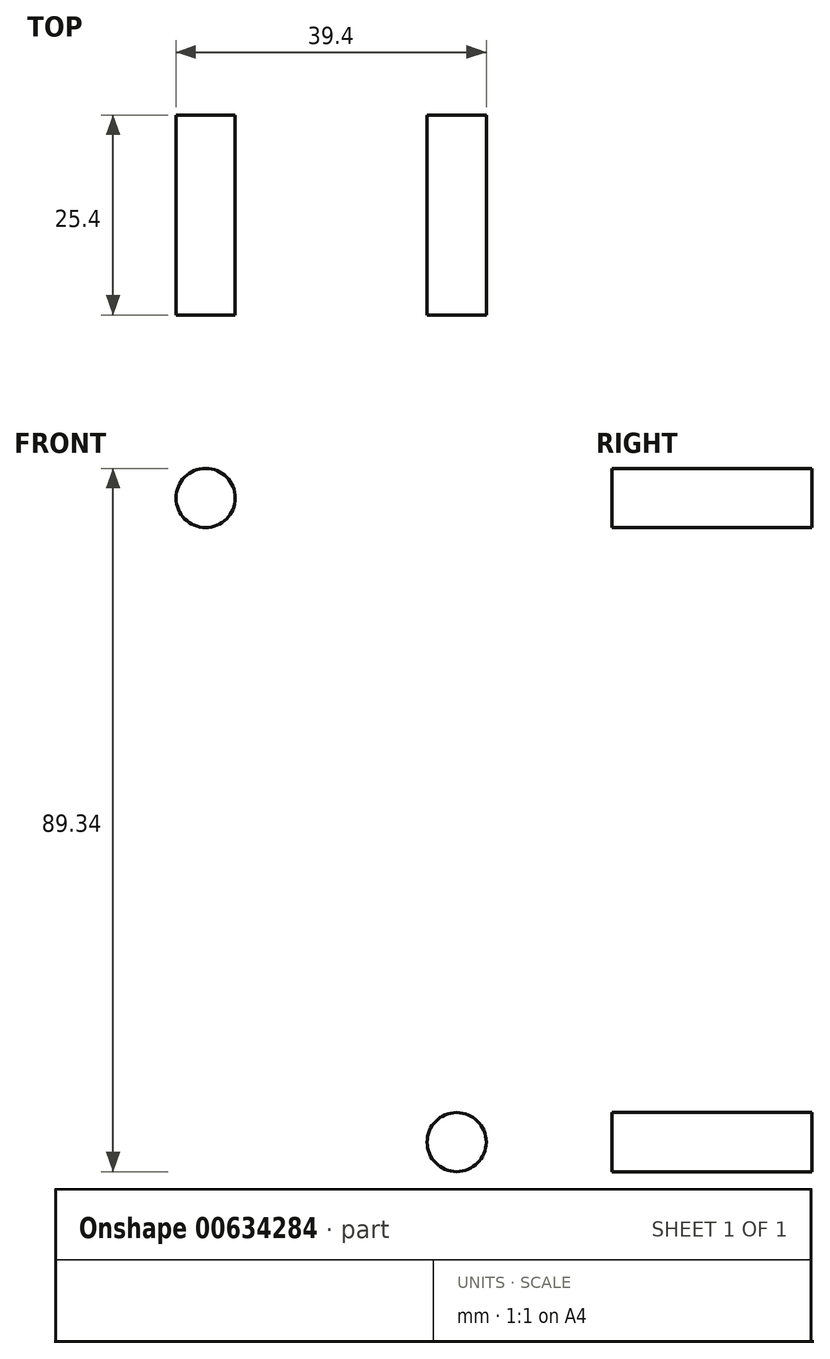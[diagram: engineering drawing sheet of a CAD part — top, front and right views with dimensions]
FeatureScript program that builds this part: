
annotation { "Feature Type Name" : "Feature", "Feature Type Description" : "" }
export const myFeature = defineFeature(function(context is Context, id is Id, definition is map)
    precondition{}
    {
        {
            var Q0;
            Q0=qCreatedBy(makeId("Front.planeOp"),FACE);
            var sketch = newSketch(context, id + "F0", { "sketchPlane" : qUnion([Q0])});
            skLineSegment(sketch, "E0.bottom", {"start": v(-25.4, -50.8) * mm, "end": v(25.4, -50.8) * mm});
            skLineSegment(sketch, "E0.top", {"start": v(-25.4, 50.8) * mm, "end": v(25.4, 50.8) * mm});
            skLineSegment(sketch, "E0.left", {"start": v(-25.4, -50.8) * mm, "end": v(-25.4, 50.8) * mm});
            skLineSegment(sketch, "E0.right", {"start": v(25.4, -50.8) * mm, "end": v(25.4, 50.8) * mm});
            skPoint(sketch, "E0.middle", {"position": v(0, 0) * mm});
            skCircle(sketch, "E1", {"center": v(0, -26.93) * mm, "radius": 7.62 * mm});
            skPoint(sketch, "E1.centerSnap0", {"position": v(0, 50.8) * mm});
            skCircle(sketch, "E2.MirrorC", {"center": v(0, 26.93) * mm, "radius": 7.62 * mm});
            skSolve(sketch);
        }
        {
            var Q0;
            Q0=makeQuery(id+"F0.imprint","IMPRINT",FACE,{"disambiguationData":[TD([[makeQuery(id+"F0.imprint","IMPRINT",EDGE,{"derivedFrom":sQuery(id+"F0.wireOp",EDGE,"E0.bottom")}),1.0]])]});
            extrude(context, id + "F1", {"entities" : qUnion([Q0]), "depth" : 25.4 * mm, "offsetDistance" : 25.4 * mm});
        }
        {
            var Q0;
            Q0=makeQuery(id+"F1.opExtrude","SWEPT_EDGE",EDGE,{"disambiguationData":[OSD([sQuery(id+"F0.wireOp",EDGE,"E0.bottom"),sQuery(id+"F0.wireOp",EDGE,"E0.right")])]});
            var Q1;
            Q1=makeQuery(id+"F1.opExtrude","SWEPT_EDGE",EDGE,{"disambiguationData":[OSD([sQuery(id+"F0.wireOp",EDGE,"E0.top"),sQuery(id+"F0.wireOp",EDGE,"E0.right")])]});
            var Q2;
            Q2=makeQuery(id+"F1.opExtrude","SWEPT_EDGE",EDGE,{"disambiguationData":[OSD([sQuery(id+"F0.wireOp",EDGE,"E0.top"),sQuery(id+"F0.wireOp",EDGE,"E0.left")])]});
            var Q3;
            Q3=makeQuery(id+"F1.opExtrude","SWEPT_EDGE",EDGE,{"disambiguationData":[OSD([sQuery(id+"F0.wireOp",EDGE,"E0.bottom"),sQuery(id+"F0.wireOp",EDGE,"E0.left")])]});
            fillet(context, id + "F2", {"entities" : qUnion([Q0, Q1, Q2, Q3]), "radius" : 5.08 * mm, "tangentPropagation" : true, "allowEdgeOverflow" : false});
        }
        {
            var Q0;
            Q0=makeQuery(id+"F1.opExtrude","CAP_FACE",FACE,{"disambiguationData":[OSD([sQuery(id+"F0.wireOp",EDGE,"E0.bottom"),sQuery(id+"F0.wireOp",EDGE,"E0.top"),sQuery(id+"F0.wireOp",EDGE,"E0.left"),sQuery(id+"F0.wireOp",EDGE,"E0.right"),sQuery(id+"F0.wireOp",EDGE,"E1"),sQuery(id+"F0.wireOp",EDGE,"E2.MirrorC")])],"isStart":true});
            var sketch = newSketch(context, id + "F3", { "sketchPlane" : qUnion([Q0])});
            skCircle(sketch, "E3", {"center": v(-15.95, 40.92) * mm, "radius": 3.75 * mm});
            skCircle(sketch, "E4.MirrorC", {"center": v(15.95, 40.92) * mm, "radius": 3.75 * mm});
            skCircle(sketch, "E5.MirrorC", {"center": v(-15.95, -40.92) * mm, "radius": 3.75 * mm});
            skCircle(sketch, "E6.MirrorC", {"center": v(15.95, -40.92) * mm, "radius": 3.75 * mm});
            skSolve(sketch);
        }
        {
            var Q0;
            Q0=makeQuery(id+"F3.imprint","IMPRINT",FACE,{"disambiguationData":[TD([[makeQuery(id+"F3.imprint","IMPRINT",EDGE,{"derivedFrom":sQuery(id+"F3.wireOp",EDGE,"E3")}),1.0]])]});
            var Q1;
            Q1=makeQuery(id+"F3.imprint","IMPRINT",FACE,{"disambiguationData":[TD([[makeQuery(id+"F3.imprint","IMPRINT",EDGE,{"derivedFrom":sQuery(id+"F3.wireOp",EDGE,"E4.MirrorC")}),-1.0]])]});
            var Q2;
            Q2=makeQuery(id+"F3.imprint","IMPRINT",FACE,{"disambiguationData":[TD([[makeQuery(id+"F3.imprint","IMPRINT",EDGE,{"derivedFrom":sQuery(id+"F3.wireOp",EDGE,"E6.MirrorC")}),1.0]])]});
            var Q3;
            Q3=makeQuery(id+"F3.imprint","IMPRINT",FACE,{"disambiguationData":[TD([[makeQuery(id+"F3.imprint","IMPRINT",EDGE,{"derivedFrom":sQuery(id+"F3.wireOp",EDGE,"E5.MirrorC")}),-1.0]])]});
            extrude(context, id + "F4", {"entities" : qUnion([Q0, Q1, Q2, Q3]), "operationType" : NewBodyOperationType.REMOVE, "oppositeDirection" : true, "depth" : 25.4 * mm, "offsetDistance" : 25.4 * mm});
        }
    });
